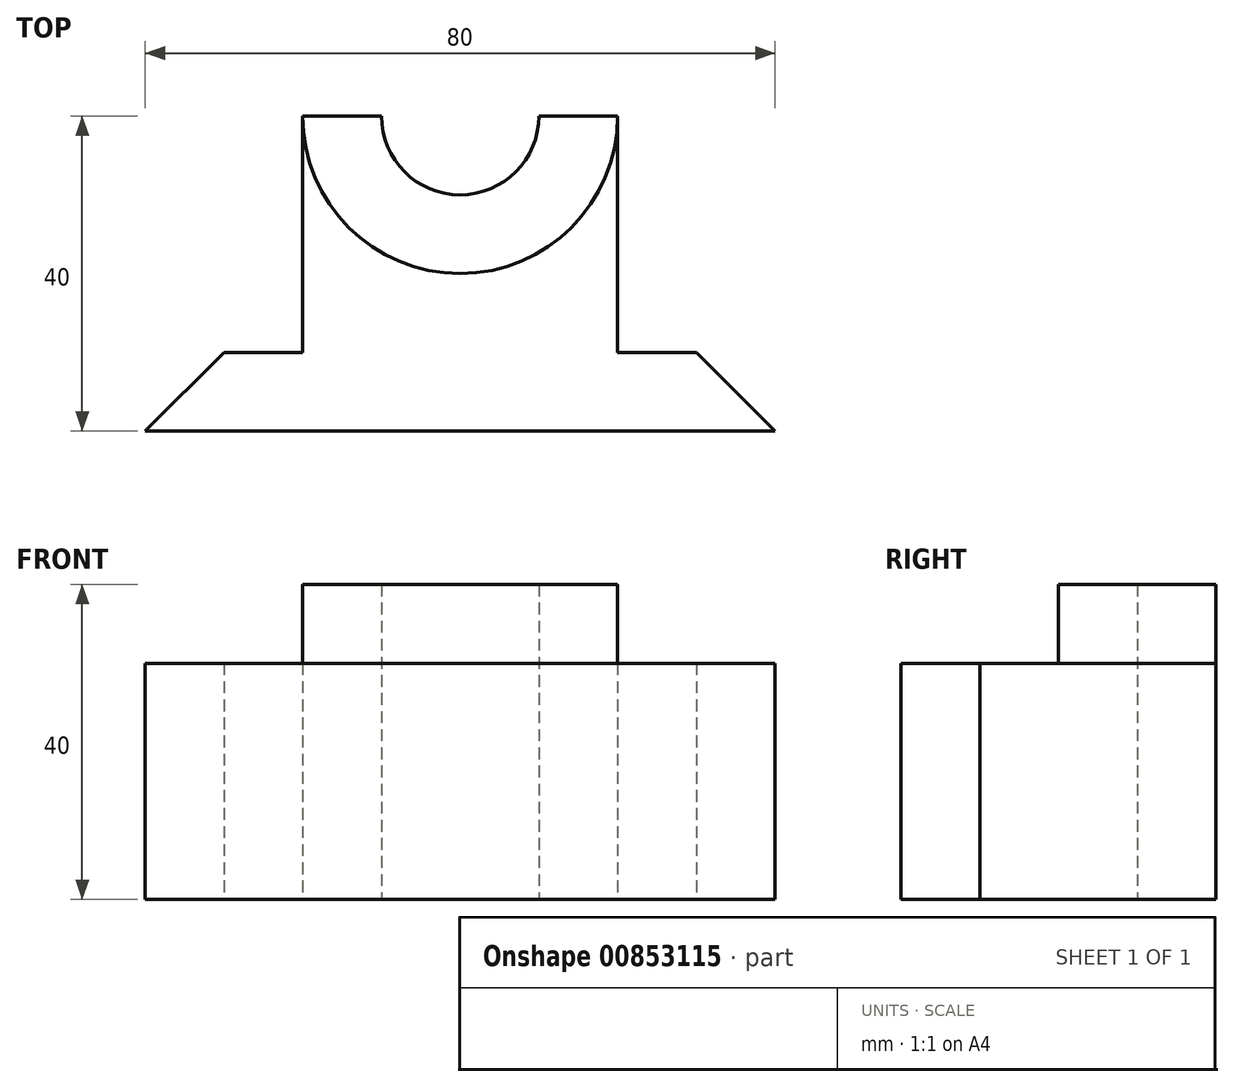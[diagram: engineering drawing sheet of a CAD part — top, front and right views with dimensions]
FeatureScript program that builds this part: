
annotation { "Feature Type Name" : "Feature", "Feature Type Description" : "" }
export const myFeature = defineFeature(function(context is Context, id is Id, definition is map)
    precondition{}
    {
        {
            var Q0;
            Q0=qCreatedBy(makeId("Top.planeOp"),FACE);
            var sketch = newSketch(context, id + "F0", { "sketchPlane" : qUnion([Q0])});
            skLineSegment(sketch, "E0", {"start": v(0, 0) * mm, "end": v(40, 0) * mm});
            skLineSegment(sketch, "E1", {"start": v(20, 40) * mm, "end": v(20, 40) * mm});
            skLineSegment(sketch, "E2", {"start": v(0, 20) * mm, "end": v(0, 20) * mm});
            skPoint(sketch, "E3.visualSharp", {"position": v(20, 20) * mm});
            skArc(sketch, "E3.filletArc", {"start": v(0, 20) * mm, "mid": v(14.14, 25.86) * mm, "end": v(20, 40) * mm});
            skLineSegment(sketch, "E4", {"start": v(10, 40) * mm, "end": v(10, 40) * mm});
            skLineSegment(sketch, "E5", {"start": v(0, 30) * mm, "end": v(0, 30) * mm});
            skPoint(sketch, "E6.visualSharp", {"position": v(10, 30) * mm});
            skArc(sketch, "E6.filletArc", {"start": v(0, 30) * mm, "mid": v(7.07, 32.93) * mm, "end": v(10, 40) * mm});
            skLineSegment(sketch, "E7", {"start": v(20, 10) * mm, "end": v(20, 40) * mm});
            skLineSegment(sketch, "E8.MirrorCS", {"start": v(0, 0) * mm, "end": v(-40, 0) * mm});
            skLineSegment(sketch, "E9.MirrorCS", {"start": v(-20, 10) * mm, "end": v(-20, 40) * mm});
            skArc(sketch, "E10.MirrorCS", {"start": v(0, 20) * mm, "mid": v(-14.14, 25.86) * mm, "end": v(-20, 40) * mm});
            skArc(sketch, "E11.MirrorCS", {"start": v(0, 30) * mm, "mid": v(-7.07, 32.93) * mm, "end": v(-10, 40) * mm});
            skLineSegment(sketch, "E12", {"start": v(-20, 40) * mm, "end": v(-10, 40) * mm});
            skLineSegment(sketch, "E13", {"start": v(10, 40) * mm, "end": v(20, 40) * mm});
            skLineSegment(sketch, "E14", {"start": v(40, 0) * mm, "end": v(30, 0) * mm});
            skLineSegment(sketch, "E15", {"start": v(40, 0) * mm, "end": v(30, 10) * mm});
            skLineSegment(sketch, "E16", {"start": v(30, 10) * mm, "end": v(20, 10) * mm});
            skLineSegment(sketch, "E17", {"start": v(-30, 10) * mm, "end": v(-40, 0) * mm});
            skLineSegment(sketch, "E18", {"start": v(-30, 10) * mm, "end": v(-20, 10) * mm});
            skSolve(sketch);
        }
        {
            var Q0;
            Q0=makeQuery(id+"F0.imprint","IMPRINT",FACE,{"disambiguationData":[TD([[makeQuery(id+"F0.imprint","IMPRINT",EDGE,{"derivedFrom":sQuery(id+"F0.wireOp",EDGE,"E0")}),1.0]])]});
            extrude(context, id + "F1", {"entities" : qUnion([Q0]), "depth" : 30 * mm, "offsetDistance" : 25 * mm});
        }
        {
            var Q0;
            Q0=makeQuery(id+"F0.imprint","IMPRINT",FACE,{"disambiguationData":[TD([[makeQuery(id+"F0.imprint","IMPRINT",EDGE,{"derivedFrom":sQuery(id+"F0.wireOp",EDGE,"E3.filletArc")}),1.0]])]});
            extrude(context, id + "F2", {"entities" : qUnion([Q0]), "operationType" : NewBodyOperationType.ADD, "depth" : 40 * mm, "offsetDistance" : 25 * mm});
        }
    });
